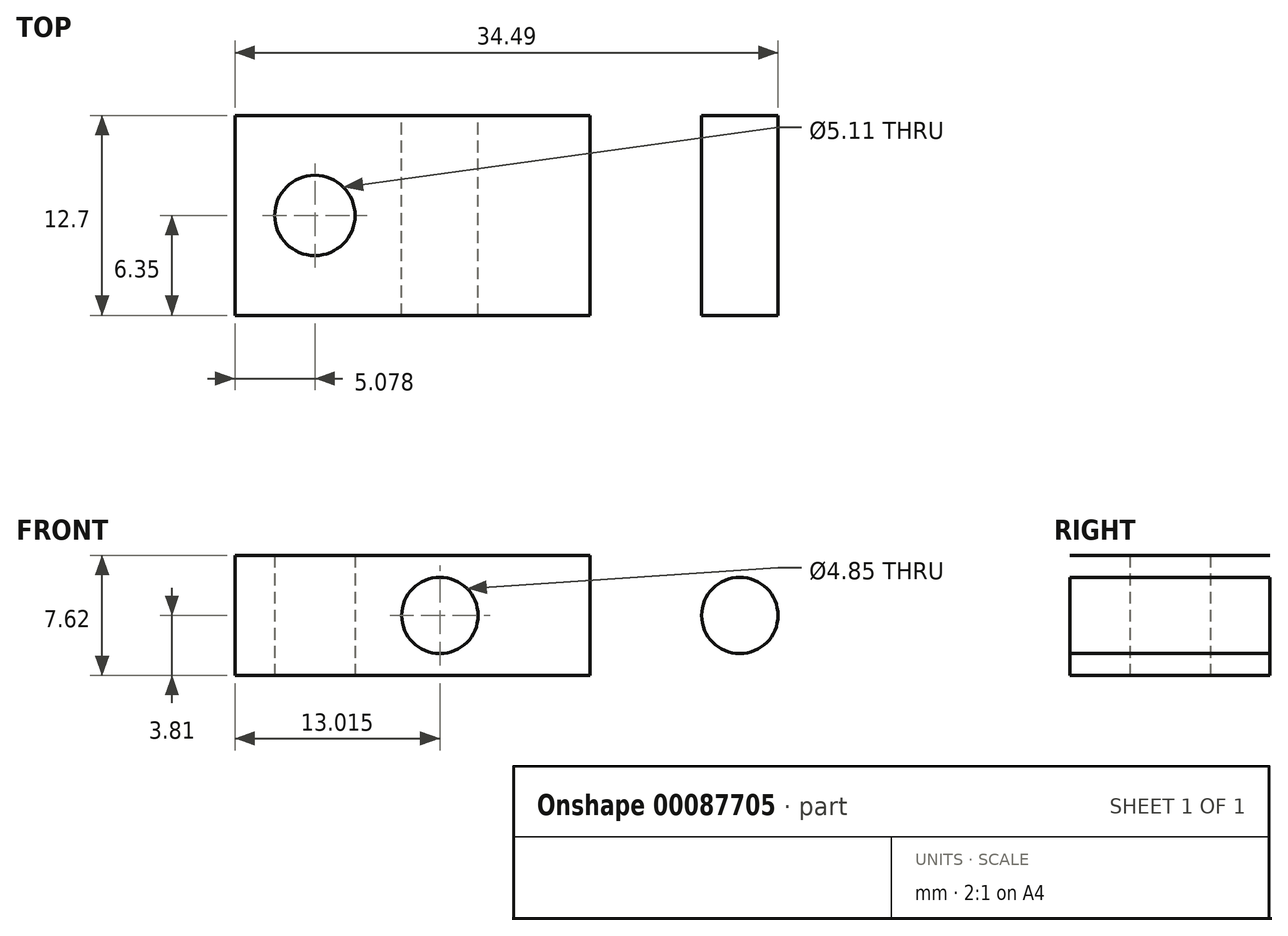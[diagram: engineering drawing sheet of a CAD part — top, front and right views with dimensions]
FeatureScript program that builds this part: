
annotation { "Feature Type Name" : "Feature", "Feature Type Description" : "" }
export const myFeature = defineFeature(function(context is Context, id is Id, definition is map)
    precondition{}
    {
        {
            var Q0;
            Q0=qCreatedBy(makeId("Top.planeOp"),FACE);
            var sketch = newSketch(context, id + "F0", { "sketchPlane" : qUnion([Q0])});
            skLineSegment(sketch, "E0.bottom", {"start": v(-22.54, 6.35) * mm, "end": v(22.54, 6.35) * mm});
            skLineSegment(sketch, "E0.top", {"start": v(-22.54, -6.35) * mm, "end": v(22.54, -6.35) * mm});
            skLineSegment(sketch, "E0.left", {"start": v(-22.54, 6.35) * mm, "end": v(-22.54, -6.35) * mm});
            skLineSegment(sketch, "E0.right", {"start": v(22.54, 6.35) * mm, "end": v(22.54, -6.35) * mm});
            skPoint(sketch, "E0.middle", {"position": v(0, 0) * mm});
            skLineSegment(sketch, "E1", {"start": v(25.33, 0) * mm, "end": v(-34.84, 0) * mm});
            skCircle(sketch, "E2", {"center": v(-17.46, 0) * mm, "radius": 2.55 * mm});
            skCircle(sketch, "E3", {"center": v(17.46, 0) * mm, "radius": 2.55 * mm});
            skLineSegment(sketch, "E4", {"start": v(0, 18.51) * mm, "end": v(0, -12.43) * mm});
            skSolve(sketch);
        }
        {
            var Q0;
            Q0 = qSketchRegion(id + "F0", true);
            extrude(context, id + "F1", {"entities" : qUnion([Q0]), "depth" : 7.62 * mm});
        }
        {
            var Q0;
            Q0=makeQuery(id+"F1.opExtrude","SWEPT_FACE",FACE,{"disambiguationData":[OSD([sQuery(id+"F0.wireOp",EDGE,"E0.bottom")])]});
            var sketch = newSketch(context, id + "F2", { "sketchPlane" : qUnion([Q0])});
            skLineSegment(sketch, "E5", {"start": v(25.48, 3.81) * mm, "end": v(-25.14, 3.81) * mm});
            skPoint(sketch, "E5.startSnap0", {"position": v(22.54, 3.81) * mm});
            skCircle(sketch, "E6", {"center": v(-9.53, 3.8) * mm, "radius": 2.43 * mm});
            skCircle(sketch, "E7", {"center": v(9.53, 3.8) * mm, "radius": 2.43 * mm});
            skLineSegment(sketch, "E8", {"start": v(0, 11.47) * mm, "end": v(0, -2.95) * mm});
            skPoint(sketch, "E8.startSnap0", {"position": v(0, 7.62) * mm});
            skSolve(sketch);
        }
        {
            var Q0;
            {var subQ0=sQuery(id+"F2.wireOp",EDGE,"E6");var subQ1=sQuery(id+"F2.wireOp",EDGE,"E5");var subQ2=makeQuery(id+"F2.imprint","INTERSECT",VERTEX,{"disambiguationData":[OD(0.0)],"derivedFrom":[subQ1,subQ0]});Q0=makeQuery(id+"F2.imprint","IMPRINT",FACE,{"disambiguationData":[TD([[makeQuery(id+"F2.imprint","IMPRINT",EDGE,{"disambiguationData":[TD([[subQ2,-1.0]])],"derivedFrom":subQ1}),-1.0]])]});}
            var Q1;
            {var subQ0=sQuery(id+"F2.wireOp",EDGE,"E6");var subQ1=sQuery(id+"F2.wireOp",EDGE,"E5");var subQ2=makeQuery(id+"F2.imprint","INTERSECT",VERTEX,{"disambiguationData":[OD(0.0)],"derivedFrom":[subQ1,subQ0]});Q1=makeQuery(id+"F2.imprint","IMPRINT",FACE,{"disambiguationData":[TD([[makeQuery(id+"F2.imprint","IMPRINT",EDGE,{"disambiguationData":[TD([[subQ2,-1.0]])],"derivedFrom":subQ1}),1.0]])]});}
            var Q2;
            {var subQ0=sQuery(id+"F2.wireOp",EDGE,"E7");var subQ1=sQuery(id+"F2.wireOp",EDGE,"E5");var subQ2=makeQuery(id+"F2.imprint","INTERSECT",VERTEX,{"disambiguationData":[OD(0.0)],"derivedFrom":[subQ1,subQ0]});Q2=makeQuery(id+"F2.imprint","IMPRINT",FACE,{"disambiguationData":[TD([[makeQuery(id+"F2.imprint","IMPRINT",EDGE,{"disambiguationData":[TD([[subQ2,-1.0]])],"derivedFrom":subQ1}),1.0]])]});}
            var Q3;
            {var subQ0=sQuery(id+"F2.wireOp",EDGE,"E7");var subQ1=sQuery(id+"F2.wireOp",EDGE,"E5");var subQ2=makeQuery(id+"F2.imprint","INTERSECT",VERTEX,{"disambiguationData":[OD(0.0)],"derivedFrom":[subQ1,subQ0]});Q3=makeQuery(id+"F2.imprint","IMPRINT",FACE,{"disambiguationData":[TD([[makeQuery(id+"F2.imprint","IMPRINT",EDGE,{"disambiguationData":[TD([[subQ2,-1.0]])],"derivedFrom":subQ1}),-1.0]])]});}
            extrude(context, id + "F3", {"entities" : qUnion([Q0, Q1, Q2, Q3]), "operationType" : NewBodyOperationType.REMOVE, "oppositeDirection" : true, "depth" : 25.4 * mm});
        }
    });
